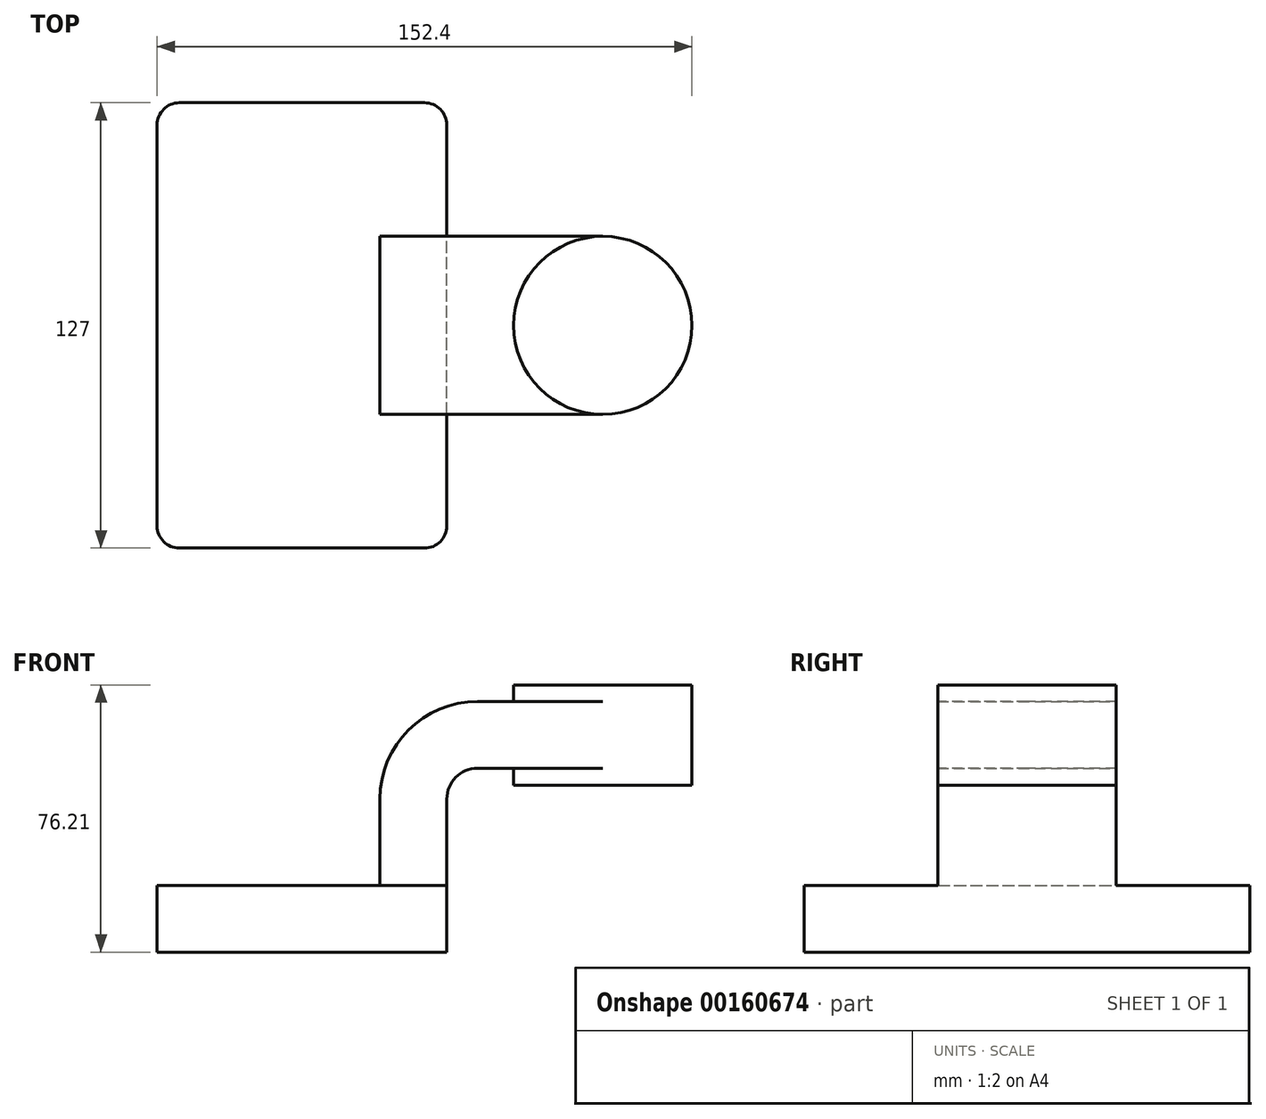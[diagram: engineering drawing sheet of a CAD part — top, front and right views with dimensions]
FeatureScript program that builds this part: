
annotation { "Feature Type Name" : "Feature", "Feature Type Description" : "" }
export const myFeature = defineFeature(function(context is Context, id is Id, definition is map)
    precondition{}
    {
        {
            var Q0;
            Q0=qCreatedBy(makeId("Front.planeOp"),FACE);
            var sketch = newSketch(context, id + "F0", { "sketchPlane" : qUnion([Q0])});
            skLineSegment(sketch, "E0.bottom", {"start": v(41.28, -9.52) * mm, "end": v(-41.27, -9.52) * mm});
            skLineSegment(sketch, "E0.top", {"start": v(41.27, 9.53) * mm, "end": v(-41.28, 9.53) * mm});
            skLineSegment(sketch, "E0.left", {"start": v(41.28, -9.52) * mm, "end": v(41.28, 9.53) * mm});
            skLineSegment(sketch, "E0.right", {"start": v(-41.27, -9.52) * mm, "end": v(-41.28, 9.53) * mm});
            skPoint(sketch, "E0.middle", {"position": v(0, 0) * mm});
            skLineSegment(sketch, "E1.bottom", {"start": v(111.12, 38.1) * mm, "end": v(60.32, 38.1) * mm});
            skLineSegment(sketch, "E1.top", {"start": v(111.12, 66.68) * mm, "end": v(60.32, 66.68) * mm});
            skLineSegment(sketch, "E1.left", {"start": v(111.12, 38.1) * mm, "end": v(111.12, 66.68) * mm});
            skLineSegment(sketch, "E1.right", {"start": v(60.32, 38.1) * mm, "end": v(60.32, 66.68) * mm});
            skPoint(sketch, "E1.middle", {"position": v(85.72, 52.39) * mm});
            skLineSegment(sketch, "E2", {"start": v(41.27, 9.53) * mm, "end": v(41.27, 34.15) * mm});
            skArc(sketch, "E3", {"start": v(41.27, 34.15) * mm, "mid": v(43.83, 40.32) * mm, "end": v(50, 42.88) * mm});
            skLineSegment(sketch, "E4", {"start": v(50, 42.88) * mm, "end": v(85.72, 42.88) * mm});
            skLineSegment(sketch, "E5.0", {"start": v(50, 61.93) * mm, "end": v(85.72, 61.93) * mm});
            skArc(sketch, "E5.1", {"start": v(22.22, 34.15) * mm, "mid": v(30.36, 53.8) * mm, "end": v(50, 61.93) * mm});
            skLineSegment(sketch, "E5.2", {"start": v(22.22, 9.53) * mm, "end": v(22.22, 34.15) * mm});
            skLineSegment(sketch, "E6", {"start": v(85.72, 38.1) * mm, "end": v(85.72, 66.68) * mm});
            skFitSpline(sketch, "E7", {"points": [v(-41.28, 9.52) * mm, v(60.32, 61.93) * mm], "startDerivative": vector(37.68, 77.8) * mm, "endDerivative": vector(166.06, -15.01) * mm});
            skSolve(sketch);
        }
        {
            var Q0;
            Q0=makeQuery(id+"F0.imprint","IMPRINT",FACE,{"disambiguationData":[TD([[makeQuery(id+"F0.imprint","IMPRINT",EDGE,{"derivedFrom":sQuery(id+"F0.wireOp",EDGE,"E0.bottom")}),-1.0]])]});
            extrude(context, id + "F1", {"entities" : qUnion([Q0]), "endBound" : BoundingType.SYMMETRIC, "depth" : 127 * mm});
        }
        {
            var Q0;
            {var subQ1=sQuery(id+"F0.wireOp",EDGE,"E2");Q0=makeQuery(id+"F0.imprint","IMPRINT",FACE,{"disambiguationData":[TD([[makeQuery(id+"F0.imprint","IMPRINT",EDGE,{"derivedFrom":subQ1}),1.0]])]});}
            var Q1;
            {var subQ3=sQuery(id+"F0.wireOp",EDGE,"E4");var subQ5=sQuery(id+"F0.wireOp",EDGE,"E6");var subQ6=makeQuery(id+"F0.imprint","INTERSECT",VERTEX,{"derivedFrom":[subQ3,subQ5]});Q1=makeQuery(id+"F0.imprint","IMPRINT",FACE,{"disambiguationData":[TD([[makeQuery(id+"F0.imprint","IMPRINT",EDGE,{"disambiguationData":[TD([[subQ6,1.0]])],"derivedFrom":subQ3}),1.0]])]});}
            extrude(context, id + "F2", {"entities" : qUnion([Q0, Q1]), "operationType" : NewBodyOperationType.ADD, "endBound" : BoundingType.SYMMETRIC, "depth" : 50.8 * mm});
        }
        {
            var Q0;
            {var subQ1=sQuery(id+"F0.wireOp",EDGE,"E5.1");Q0=makeQuery(id+"F0.imprint","IMPRINT",FACE,{"disambiguationData":[TD([[makeQuery(id+"F0.imprint","IMPRINT",EDGE,{"derivedFrom":subQ1}),1.0]])]});}
            extrude(context, id + "F3", {"entities" : qUnion([Q0]), "operationType" : NewBodyOperationType.ADD, "endBound" : BoundingType.SYMMETRIC, "depth" : 15.88 * mm});
        }
        {
            var Q0;
            {var subQ0=sQuery(id+"F0.wireOp",EDGE,"E1.left");Q0=makeQuery(id+"F0.imprint","IMPRINT",FACE,{"disambiguationData":[TD([[makeQuery(id+"F0.imprint","IMPRINT",EDGE,{"derivedFrom":subQ0}),1.0]])]});}
            var Q1;
            Q1=sQuery(id+"F0.wireOp",EDGE,"E6");
            revolve(context, id + "F4", {"operationType" : NewBodyOperationType.ADD, "entities" : qUnion([Q0]), "axis" : qUnion([Q1]), "revolveType" : RevolveType.FULL});
        }
        {
            var Q0;
            Q0=makeQuery(id+"F1.opExtrude","CAP_EDGE",EDGE,{"disambiguationData":[OSD([sQuery(id+"F0.wireOp",EDGE,"E0.left")])],"isStart":false});
            var Q1;
            Q1=makeQuery(id+"F1.opExtrude","CAP_EDGE",EDGE,{"disambiguationData":[OSD([sQuery(id+"F0.wireOp",EDGE,"E0.right")])],"isStart":false});
            var Q2;
            Q2=makeQuery(id+"F1.opExtrude","CAP_EDGE",EDGE,{"disambiguationData":[OSD([sQuery(id+"F0.wireOp",EDGE,"E0.right")])],"isStart":true});
            var Q3;
            Q3=makeQuery(id+"F1.opExtrude","CAP_EDGE",EDGE,{"disambiguationData":[OSD([sQuery(id+"F0.wireOp",EDGE,"E0.left")])],"isStart":true});
            fillet(context, id + "F5", {"entities" : qUnion([Q0, Q1, Q2, Q3]), "radius" : 6.35 * mm, "tangentPropagation" : true, "allowEdgeOverflow" : false});
        }
    });
